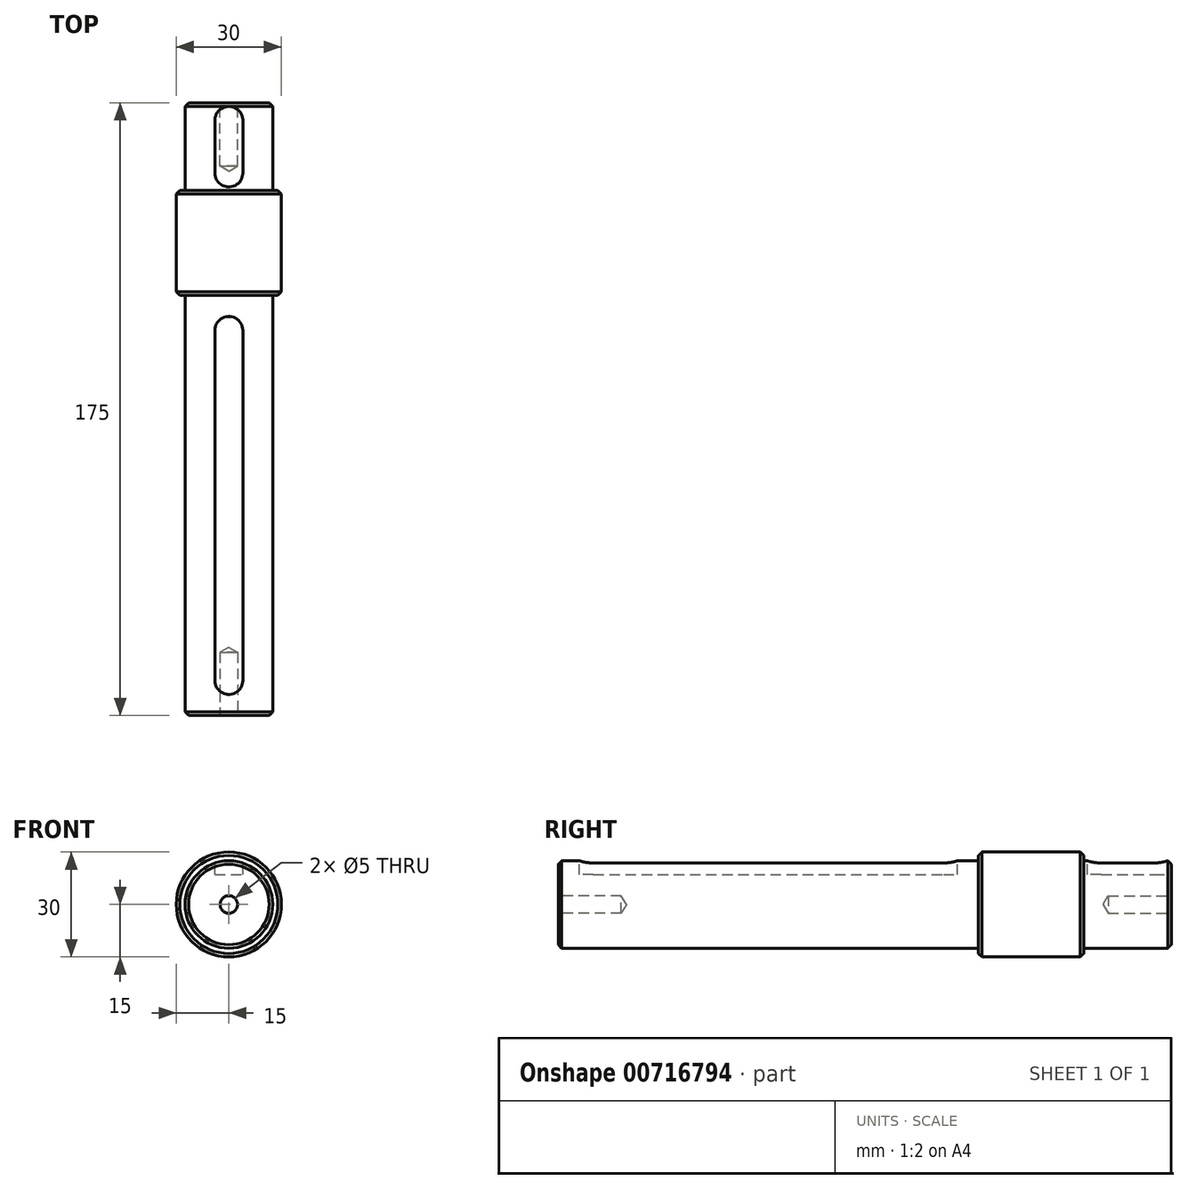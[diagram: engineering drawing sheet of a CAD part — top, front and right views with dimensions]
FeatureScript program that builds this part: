
annotation { "Feature Type Name" : "Feature", "Feature Type Description" : "" }
export const myFeature = defineFeature(function(context is Context, id is Id, definition is map)
    precondition{}
    {
        {
            var Q0;
            Q0=qCreatedBy(makeId("Right.planeOp"),FACE);
            var sketch = newSketch(context, id + "F0", { "sketchPlane" : qUnion([Q0])});
            skLineSegment(sketch, "E0", {"start": v(-87.5, 0) * mm, "end": v(87.5, 0) * mm});
            skLineSegment(sketch, "E1", {"start": v(87.5, 0) * mm, "end": v(87.5, 12.5) * mm});
            skLineSegment(sketch, "E2", {"start": v(87.5, 12.5) * mm, "end": v(62.5, 12.5) * mm});
            skLineSegment(sketch, "E3", {"start": v(62.5, 12.5) * mm, "end": v(62.5, 15) * mm});
            skLineSegment(sketch, "E4", {"start": v(62.5, 15) * mm, "end": v(32.5, 15) * mm});
            skLineSegment(sketch, "E5", {"start": v(32.5, 15) * mm, "end": v(32.5, 12.5) * mm});
            skLineSegment(sketch, "E6", {"start": v(32.5, 12.5) * mm, "end": v(-87.5, 12.5) * mm});
            skLineSegment(sketch, "E7", {"start": v(-87.5, 12.5) * mm, "end": v(-87.5, 0) * mm});
            skSolve(sketch);
        }
        {
            var Q0;
            Q0 = qSketchRegion(id + "F0", true);
            var Q1;
            Q1=sQuery(id+"F0.wireOp",EDGE,"E0");
            revolve(context, id + "F1", {"surfaceOperationType" : NewSurfaceOperationType.NEW, "entities" : qUnion([Q0]), "axis" : qUnion([Q1]), "revolveType" : RevolveType.FULL});
        }
        {
            var Q0;
            Q0=makeQuery(id+"F1.opRevolve","SWEPT_FACE",FACE,{"disambiguationData":[OSD([sQuery(id+"F0.wireOp",EDGE,"E7")])]});
            var sketch = newSketch(context, id + "F2", { "sketchPlane" : qUnion([Q0])});
            skPoint(sketch, "E8", {"position": v(0, 0) * mm});
            skSolve(sketch);
        }
        {
            var Q0;
            Q0=makeQuery(id+"F1.opRevolve","SWEPT_FACE",FACE,{"disambiguationData":[OSD([sQuery(id+"F0.wireOp",EDGE,"E1")])]});
            var sketch = newSketch(context, id + "F3", { "sketchPlane" : qUnion([Q0])});
            skPoint(sketch, "E9", {"position": v(0, 0) * mm});
            skSolve(sketch);
        }
        {
            var Q0;
            Q0=sQuery(id+"F2.wireOp",VERTEX,"E8");
            var Q1;
            Q1=sQuery(id+"F3.wireOp",VERTEX,"E9");
            var Q2;
            Q2=makeQuery(id+"F1.opRevolve","SWEPT_BODY",BODY,{"disambiguationData":[OSD([sQuery(id+"F0.wireOp",EDGE,"E0"),sQuery(id+"F0.wireOp",EDGE,"E1"),sQuery(id+"F0.wireOp",EDGE,"E2"),sQuery(id+"F0.wireOp",EDGE,"E3"),sQuery(id+"F0.wireOp",EDGE,"E4"),sQuery(id+"F0.wireOp",EDGE,"E5"),sQuery(id+"F0.wireOp",EDGE,"E6"),sQuery(id+"F0.wireOp",EDGE,"E7")])]});
            hole(context, id + "F4", {"style" : HoleStyle.SIMPLE, "endStyle" : HoleEndStyle.BLIND, "standardTappedOrClearance" : lookupTablePath({ "standard" : "ISO", "engagement" : "75%", "pitch" : "1 mm", "size" : "M6", "type" : "Tapped" }), "standardBlindInLast" : lookupTablePath({ "standard" : "ISO", "engagement" : "75%", "pitch" : "1 mm", "size" : "M6", "type" : "Tapped" }), "holeDiameter" : 5 * mm, "majorDiameter" : 6 * mm, "showTappedDepth" : true, "holeDepth" : 18 * mm, "isTappedThrough" : true, "tappedDepth" : 15 * mm, "tapClearance" : 3, "startFromSketch" : true, "locations" : qUnion([Q0, Q1]), "scope" : qUnion([Q2])});
        }
        {
            var Q0;
            Q0=makeQuery(id+"F1.opRevolve","SWEPT_EDGE",EDGE,{"disambiguationData":[OSD([sQuery(id+"F0.wireOp",EDGE,"E6"),sQuery(id+"F0.wireOp",EDGE,"E7")])]});
            var Q1;
            Q1=makeQuery(id+"F1.opRevolve","SWEPT_EDGE",EDGE,{"disambiguationData":[OSD([sQuery(id+"F0.wireOp",EDGE,"E1"),sQuery(id+"F0.wireOp",EDGE,"E2")])]});
            var Q2;
            Q2=makeQuery(id+"F1.opRevolve","SWEPT_EDGE",EDGE,{"disambiguationData":[OSD([sQuery(id+"F0.wireOp",EDGE,"E4"),sQuery(id+"F0.wireOp",EDGE,"E5")])]});
            var Q3;
            Q3=makeQuery(id+"F1.opRevolve","SWEPT_EDGE",EDGE,{"disambiguationData":[OSD([sQuery(id+"F0.wireOp",EDGE,"E3"),sQuery(id+"F0.wireOp",EDGE,"E4")])]});
            chamfer(context, id + "F5", {"entities" : qUnion([Q0, Q1, Q2, Q3]), "width" : 1 * mm, "tangentPropagation" : true});
        }
        {
            var Q0;
            Q0=qCreatedBy(makeId("Top.planeOp"),FACE);
            cPlane(context, id + "F6", {"entities" : qUnion([Q0]), "cplaneType" : CPlaneType.OFFSET, "offset" : 12.5 * mm, "width" : 150 * mm, "height" : 150 * mm});
        }
        {
            var Q0;
            Q0=qCreatedBy(id+"F6.planeOp",FACE);
            var sketch = newSketch(context, id + "F7", { "sketchPlane" : qUnion([Q0])});
            skLineSegment(sketch, "E10", {"start": v(0, -77.5) * mm, "end": v(0, 22.5) * mm});
            skLineSegment(sketch, "E11", {"start": v(0, 67.5) * mm, "end": v(0, 82.5) * mm});
            skArc(sketch, "E12.0.startCap", {"start": v(4, -77.5) * mm, "mid": v(0, -81.5) * mm, "end": v(-4, -77.5) * mm});
            skArc(sketch, "E12.0.endCap", {"start": v(-4, 22.5) * mm, "mid": v(0, 26.5) * mm, "end": v(4, 22.5) * mm});
            skLineSegment(sketch, "E12.0.left", {"start": v(-4, -77.5) * mm, "end": v(-4, 22.5) * mm});
            skLineSegment(sketch, "E12.0.right", {"start": v(4, -77.5) * mm, "end": v(4, 22.5) * mm});
            skArc(sketch, "E12.1.startCap", {"start": v(4, 67.5) * mm, "mid": v(0, 63.5) * mm, "end": v(-4, 67.5) * mm});
            skArc(sketch, "E12.1.endCap", {"start": v(-4, 82.5) * mm, "mid": v(0, 86.5) * mm, "end": v(4, 82.5) * mm});
            skLineSegment(sketch, "E12.1.left", {"start": v(-4, 67.5) * mm, "end": v(-4, 82.5) * mm});
            skLineSegment(sketch, "E12.1.right", {"start": v(4, 67.5) * mm, "end": v(4, 82.5) * mm});
            skSolve(sketch);
        }
        {
            var Q0;
            Q0 = qSketchRegion(id + "F7", true);
            extrude(context, id + "F8", {"entities" : qUnion([Q0]), "operationType" : NewBodyOperationType.REMOVE, "oppositeDirection" : true, "depth" : 4 * mm, "offsetDistance" : 25 * mm});
        }
    });
